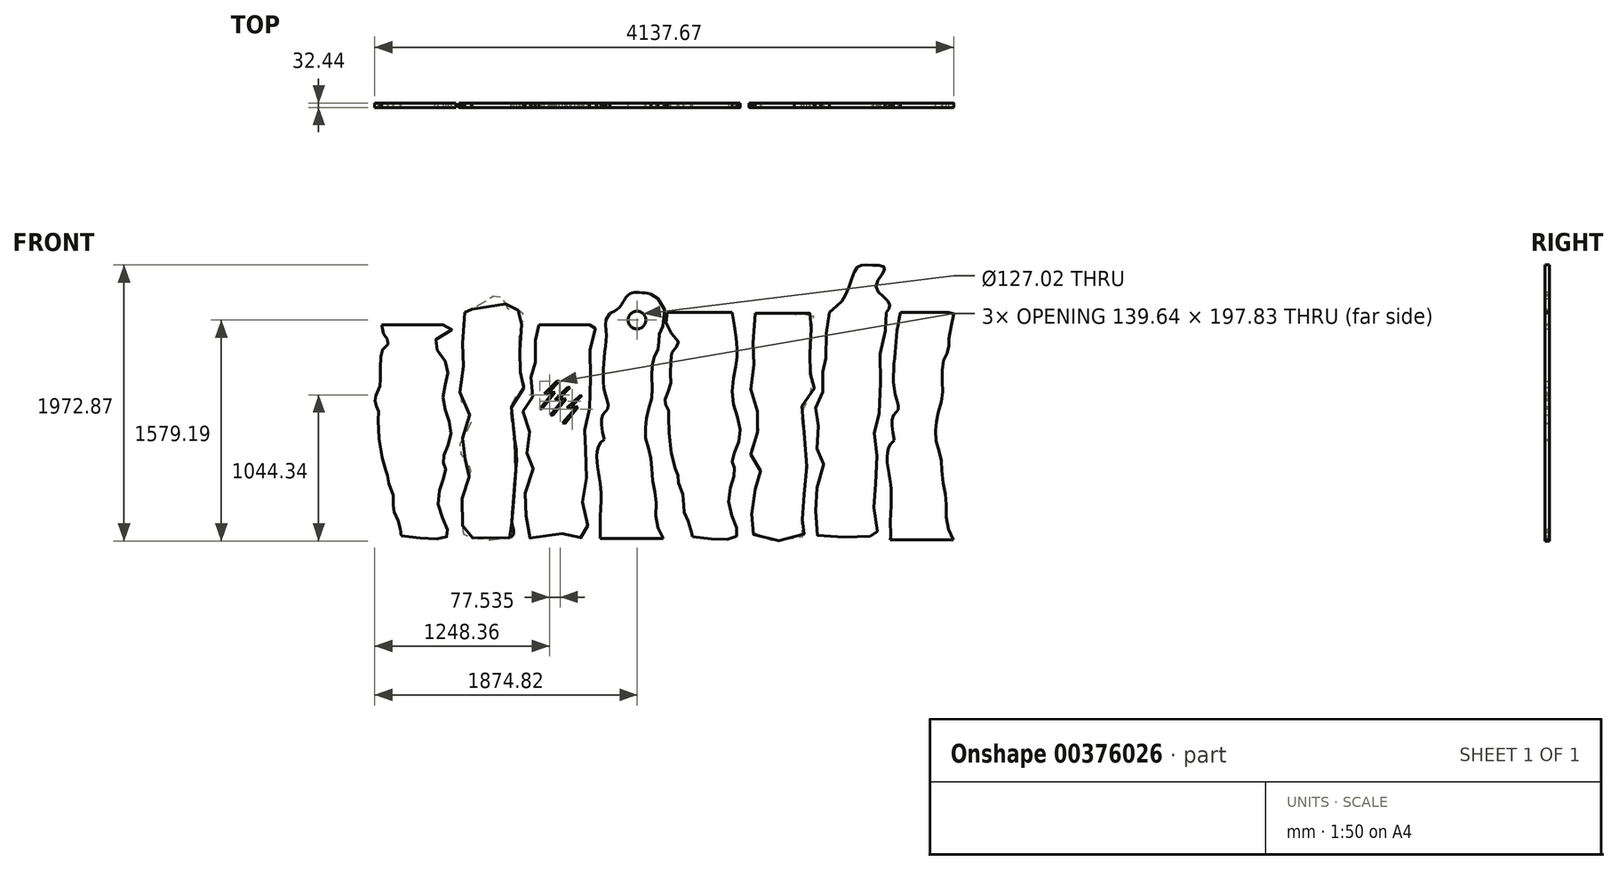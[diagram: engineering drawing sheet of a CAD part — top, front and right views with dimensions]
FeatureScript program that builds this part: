
annotation { "Feature Type Name" : "Feature", "Feature Type Description" : "" }
export const myFeature = defineFeature(function(context is Context, id is Id, definition is map)
    precondition{}
    {
        {
            var Q0;
            Q0=qCreatedBy(makeId("Front.planeOp"),FACE);
            var sketch = newSketch(context, id + "F0", { "sketchPlane" : qUnion([Q0])});
            skFitSpline(sketch, "E0", {"points": [v(-541.96, 281.1) * mm, v(-507.6, 158.34) * mm, v(-472.77, 104.36) * mm, v(-472.77, 70.55) * mm, v(-536.18, 0) * mm, v(-555.2, -90.1) * mm, v(-557.32, -301.45) * mm, v(-561.55, -390.23) * mm, v(-618.62, -523.39) * mm, v(-616.5, -555.1) * mm, v(-608.05, -599.48) * mm, v(-578.46, -660.77) * mm, v(-580.57, -730.52) * mm, v(-527.79, -1239.7) * mm, v(-480.03, -1362.86) * mm, v(-480.03, -1413.13) * mm, v(-412.16, -1626.78) * mm, v(-417.19, -1739.89) * mm, v(-379.49, -1832.9) * mm, v(-337.02, -1971.17) * mm, v(-341.75, -1975.56) * mm], "startDerivative": vector(-372.56, -2835.6) * mm, "endDerivative": vector(-506.02, -138.97) * mm});
            skLineSegment(sketch, "E1", {"start": v(-541.96, 281.1) * mm, "end": v(131.63, 281.1) * mm});
            skFitSpline(sketch, "E2", {"points": [v(131.63, 281.1) * mm, v(103, 164.5) * mm, v(170.93, -145.04) * mm, v(131.63, -522.75) * mm, v(220.27, -918.68) * mm, v(131.63, -1205.86) * mm, v(161.94, -1317.66) * mm, v(76.13, -1680.41) * mm, v(184.95, -2037.45) * mm, v(-326.9, -2043.6) * mm], "startDerivative": vector(12193.25, 0) * mm, "endDerivative": vector(-4963.23, 655.32) * mm});
            skLineSegment(sketch, "E3", {"start": v(-326.9, -2043.6) * mm, "end": v(-337.02, -1971.17) * mm});
            skLineSegment(sketch, "E4", {"start": v(-1646.42, 409.32) * mm, "end": v(-1646.42, -1190.68) * mm});
            skFitSpline(sketch, "E5", {"points": [v(371.94, 415.21) * mm, v(347.86, 0) * mm, v(355.89, -226.97) * mm, v(331.8, -556.08) * mm, v(444.19, -780.84) * mm, v(307.73, -1077.85) * mm, v(420.1, -1262.47) * mm, v(412.08, -1415) * mm, v(339.84, -1655.8) * mm, v(347.86, -1968.87) * mm, v(388, -2049.14) * mm, v(893.71, -2049.14) * mm, v(893.71, -1920.7) * mm, v(893.71, -1832.4) * mm, v(925.82, -1431.05) * mm, v(933.85, -1069.82) * mm, v(901.74, -564.1) * mm, v(1030.17, -395.54) * mm, v(990.04, -275.13) * mm, v(982.01, -106.56) * mm, v(982.01, 214.53) * mm, v(1014.12, 399.16) * mm, v(915.42, 447.26) * mm, v(834.92, 467.15) * mm, v(451.6, 447.77) * mm], "startDerivative": vector(-753, -7908.25) * mm, "endDerivative": vector(-21721.49, -16904.44) * mm});
            skLineSegment(sketch, "E6", {"start": v(451.6, 447.77) * mm, "end": v(371.94, 415.21) * mm});
            skFitSpline(sketch, "E7", {"points": [v(1189.54, 281.1) * mm, v(1159.24, 203.5) * mm, v(1151.66, -91.99) * mm, v(1136.5, -175.33) * mm, v(1098.62, -342.02) * mm, v(1113.78, -531.43) * mm, v(1015.28, -667.81) * mm, v(1083.47, -887.54) * mm, v(1053.16, -1130) * mm, v(1128.93, -1258.8) * mm, v(1038, -1561.86) * mm, v(1045.59, -1834.62) * mm, v(1106.2, -2077.08) * mm, v(1613.84, -2008.88) * mm, v(1659.3, -2077.08) * mm, v(1727.49, -1940.7) * mm, v(1666.87, -1645.2) * mm, v(1727.49, -1326.98) * mm, v(1682.03, -955.73) * mm, v(1712.33, -819.35) * mm, v(1757.8, -425.36) * mm, v(1750.22, 0) * mm, v(1812.36, 245.6) * mm, v(1818.4, 281.1) * mm, v(1746.43, 281.1) * mm], "startDerivative": vector(-915.93, -4719.56) * mm, "endDerivative": vector(-3660.24, -902.15) * mm});
            skLineSegment(sketch, "E8", {"start": v(1189.54, 281.1) * mm, "end": v(1746.43, 281.1) * mm});
            skPoint(sketch, "E9.1.internal.snap0", {"position": v(1863.87, -2077.08) * mm});
            skPoint(sketch, "E9.2.internal.snap0", {"position": v(1863.87, -2077.08) * mm});
            skFitSpline(sketch, "E9", {"points": [v(1863.87, -2077.08) * mm, v(1863.87, -1849.27) * mm, v(1863.87, -1458.06) * mm, v(1906.48, -981.8) * mm], "startDerivative": vector(45.66, 769.83) * mm, "endDerivative": vector(1037.5, 767.44) * mm});
            skFitSpline(sketch, "E10", {"points": [v(1973.4, 407.8) * mm, v(1932, 191.82) * mm, v(1914.98, 0) * mm, v(1897.98, -224.9) * mm, v(1914.98, -471.54) * mm, v(1949, -641.63) * mm, v(1889.47, -718.17) * mm, v(1906.48, -981.8) * mm], "startDerivative": vector(-1553.65, -1644.93) * mm, "endDerivative": vector(397.57, -1910.23) * mm});
            skLineSegment(sketch, "E11", {"start": v(2501.34, 569.02) * mm, "end": v(2422.34, 618.83) * mm});
            skLineSegment(sketch, "E12", {"start": v(1863.87, -2077.08) * mm, "end": v(2558.46, -2077.08) * mm});
            skFitSpline(sketch, "E13", {"points": [v(2558.46, -2077.08) * mm, v(2482.3, -1887.01) * mm, v(2477.8, -1657.25) * mm, v(2450.77, -1486.06) * mm, v(2428.25, -1269.81) * mm, v(2414.73, -1148.17) * mm, v(2365.18, -981.49) * mm, v(2365.18, -832.82) * mm, v(2378.7, -711.18) * mm, v(2428.25, -544.5) * mm, v(2437.26, -391.32) * mm, v(2432.75, -206.6) * mm, v(2459.78, -75.96) * mm, v(2495.83, 0) * mm, v(2509.34, 90.73) * mm, v(2513.85, 176.33) * mm, v(2558.46, 281.1) * mm, v(2501.34, 569.02) * mm], "startDerivative": vector(-1595.21, 2626.65) * mm, "endDerivative": vector(-3204.2, 0) * mm});
            skFitSpline(sketch, "E14", {"points": [v(2604.53, 413.66) * mm, v(2602.42, 258.18) * mm, v(2725.01, 93.31) * mm, v(2725.01, 59.5) * mm, v(2661.6, -11.05) * mm, v(2642.58, -101.14) * mm, v(2640.47, -312.5) * mm, v(2636.24, -401.28) * mm, v(2579.17, -534.44) * mm, v(2581.28, -566.14) * mm, v(2589.74, -610.53) * mm, v(2619.33, -671.82) * mm, v(2617.22, -741.58) * mm, v(2670, -1250.74) * mm, v(2717.76, -1373.9) * mm, v(2717.76, -1424.18) * mm, v(2785.62, -1637.83) * mm, v(2780.6, -1750.94) * mm, v(2818.3, -1843.94) * mm, v(2861.03, -1982.19) * mm, v(2856.04, -1986.61) * mm], "startDerivative": vector(-632.65, -2426.74) * mm, "endDerivative": vector(-506.02, -138.97) * mm});
            skLineSegment(sketch, "E15", {"start": v(2604.53, 413.66) * mm, "end": v(3318.88, 413.66) * mm});
            skFitSpline(sketch, "E16", {"points": [v(3318.88, 413.66) * mm, v(3370.75, 44.31) * mm, v(3362.77, -151.2) * mm, v(3318.88, -530.25) * mm, v(3406.66, -929.25) * mm, v(3318.88, -1216.54) * mm, v(3346.81, -1332.25) * mm, v(3278.98, -1691.35) * mm, v(3370.75, -2038.48) * mm, v(2879.98, -2054.44) * mm], "startDerivative": vector(551.1, -3340.09) * mm, "endDerivative": vector(-4963.23, 655.32) * mm});
            skLineSegment(sketch, "E17", {"start": v(2879.98, -2054.44) * mm, "end": v(2861.03, -1982.19) * mm});
            skFitSpline(sketch, "E18", {"points": [v(3569.73, 404.16) * mm, v(3545.65, -11.05) * mm, v(3553.68, -238.02) * mm, v(3529.6, -567.13) * mm, v(3641.97, -791.9) * mm, v(3505.51, -1088.9) * mm, v(3617.9, -1273.53) * mm, v(3609.87, -1426.04) * mm, v(3537.62, -1666.86) * mm, v(3545.65, -1979.92) * mm, v(3585.78, -2060.2) * mm, v(4091.5, -2060.2) * mm, v(4091.5, -1931.76) * mm, v(4091.5, -1843.46) * mm, v(4123.6, -1442.1) * mm, v(4131.63, -1080.87) * mm, v(4099.53, -575.16) * mm, v(4227.96, -406.59) * mm, v(4187.82, -286.18) * mm, v(4179.8, -117.6) * mm, v(4179.8, 203.48) * mm, v(4211.9, 388.1) * mm, v(4035.3, 404.16) * mm, v(4003.2, 404.16) * mm, v(4011.23, 404.16) * mm], "startDerivative": vector(-753, -7908.25) * mm, "endDerivative": vector(1414.6, -17.02) * mm});
            skLineSegment(sketch, "E19", {"start": v(4011.23, 404.16) * mm, "end": v(3569.73, 404.16) * mm});
            skFitSpline(sketch, "E20", {"points": [v(4387.33, 413.66) * mm, v(4357.02, 192.45) * mm, v(4349.45, -103.04) * mm, v(4334.3, -186.38) * mm, v(4296.4, -353.07) * mm, v(4311.56, -542.48) * mm, v(4213.07, -678.86) * mm, v(4281.26, -898.59) * mm, v(4250.95, -1141.04) * mm, v(4326.72, -1269.84) * mm, v(4235.8, -1572.91) * mm, v(4243.37, -1845.67) * mm, v(4303.99, -2088.12) * mm, v(4811.62, -2019.93) * mm, v(4857.08, -2088.12) * mm, v(4925.27, -1951.74) * mm, v(4864.66, -1656.25) * mm, v(4925.27, -1338.03) * mm, v(4879.81, -966.78) * mm, v(4910.12, -830.4) * mm, v(4955.58, -436.41) * mm, v(4948, -11.05) * mm, v(5016.2, 260.64) * mm, v(5016.2, 413.66) * mm, v(4944.21, 413.66) * mm], "startDerivative": vector(-915.93, -4719.56) * mm, "endDerivative": vector(-3660.24, -902.15) * mm});
            skPoint(sketch, "E21.1.internal.snap0", {"position": v(5061.65, -2088.12) * mm});
            skPoint(sketch, "E21.2.internal.snap0", {"position": v(5061.65, -2088.12) * mm});
            skFitSpline(sketch, "E21", {"points": [v(5061.65, -2088.12) * mm, v(5061.65, -1860.32) * mm, v(5061.65, -1469.11) * mm, v(5104.27, -992.86) * mm], "startDerivative": vector(45.66, 769.83) * mm, "endDerivative": vector(1037.5, 767.44) * mm});
            skFitSpline(sketch, "E22", {"points": [v(5172.3, 413.66) * mm, v(5129.78, 180.77) * mm, v(5112.77, -11.05) * mm, v(5095.76, -235.96) * mm, v(5112.77, -482.59) * mm, v(5146.79, -652.68) * mm, v(5087.26, -729.22) * mm, v(5104.27, -992.86) * mm], "startDerivative": vector(-323.99, -1499.1) * mm, "endDerivative": vector(397.57, -1910.23) * mm});
            skLineSegment(sketch, "E23", {"start": v(5699.58, 413.66) * mm, "end": v(5172.3, 413.66) * mm});
            skLineSegment(sketch, "E24", {"start": v(5061.65, -2088.12) * mm, "end": v(5756.32, -2088.12) * mm});
            skFitSpline(sketch, "E25", {"points": [v(5756.32, -2088.12) * mm, v(5680.1, -1898.07) * mm, v(5675.6, -1668.3) * mm, v(5648.56, -1497.1) * mm, v(5626.03, -1280.86) * mm, v(5612.52, -1159.23) * mm, v(5562.96, -992.54) * mm, v(5562.96, -843.87) * mm, v(5576.48, -722.23) * mm, v(5626.03, -555.54) * mm, v(5635.04, -402.37) * mm, v(5630.54, -217.66) * mm, v(5657.57, -87) * mm, v(5693.61, -11.05) * mm, v(5707.13, 79.68) * mm, v(5711.63, 165.28) * mm, v(5756.32, 413.66) * mm, v(5699.58, 413.66) * mm], "startDerivative": vector(-1595.21, 2626.65) * mm, "endDerivative": vector(-3204.22, 0) * mm});
            skFitSpline(sketch, "E26", {"points": [v(1973.4, 407.8) * mm, v(2072.73, 467.4) * mm, v(2132.33, 558.22) * mm, v(2207.53, 627.75) * mm, v(2422.34, 618.83) * mm], "startDerivative": vector(468.92, 213.8) * mm, "endDerivative": vector(767.44, -125.53) * mm});
            skCircle(sketch, "E27", {"center": v(2269.64, 331.5) * mm, "radius": 97.88 * mm});
            skLineSegment(sketch, "E28", {"start": v(1383.71, -342.02) * mm, "end": v(1245.99, -478.3) * mm});
            skLineSegment(sketch, "E29", {"start": v(1245.99, -478.3) * mm, "end": v(1329.91, -484.76) * mm});
            skLineSegment(sketch, "E30", {"start": v(1329.91, -484.76) * mm, "end": v(1196.5, -644) * mm});
            skLineSegment(sketch, "E31", {"start": v(1196.5, -644) * mm, "end": v(1223.52, -645.3) * mm});
            skLineSegment(sketch, "E32", {"start": v(1223.52, -645.3) * mm, "end": v(1367.38, -467.05) * mm});
            skLineSegment(sketch, "E33", {"start": v(1367.38, -467.05) * mm, "end": v(1294.1, -462.53) * mm});
            skLineSegment(sketch, "E34", {"start": v(1294.1, -462.53) * mm, "end": v(1411.72, -340.38) * mm});
            skLineSegment(sketch, "E35", {"start": v(1411.72, -340.38) * mm, "end": v(1383.71, -342.02) * mm});
            skLineSegment(sketch, "E36", {"start": v(1503.21, -411.76) * mm, "end": v(1365.49, -548.05) * mm});
            skLineSegment(sketch, "E37", {"start": v(1365.49, -548.05) * mm, "end": v(1449.41, -554.5) * mm});
            skLineSegment(sketch, "E38", {"start": v(1449.41, -554.5) * mm, "end": v(1316, -713.75) * mm});
            skLineSegment(sketch, "E39", {"start": v(1316, -713.75) * mm, "end": v(1343.02, -715.04) * mm});
            skLineSegment(sketch, "E40", {"start": v(1343.02, -715.04) * mm, "end": v(1486.88, -536.8) * mm});
            skLineSegment(sketch, "E41", {"start": v(1486.88, -536.8) * mm, "end": v(1413.6, -532.28) * mm});
            skLineSegment(sketch, "E42", {"start": v(1413.6, -532.28) * mm, "end": v(1531.22, -410.13) * mm});
            skLineSegment(sketch, "E43", {"start": v(1531.22, -410.13) * mm, "end": v(1503.21, -411.76) * mm});
            skLineSegment(sketch, "E44", {"start": v(1636.63, -501.91) * mm, "end": v(1498.9, -638.2) * mm});
            skLineSegment(sketch, "E45", {"start": v(1498.9, -638.2) * mm, "end": v(1582.83, -644.65) * mm});
            skLineSegment(sketch, "E46", {"start": v(1582.83, -644.65) * mm, "end": v(1449.41, -803.9) * mm});
            skLineSegment(sketch, "E47", {"start": v(1449.41, -803.9) * mm, "end": v(1476.44, -805.19) * mm});
            skLineSegment(sketch, "E48", {"start": v(1476.44, -805.19) * mm, "end": v(1620.3, -626.95) * mm});
            skLineSegment(sketch, "E49", {"start": v(1620.3, -626.95) * mm, "end": v(1547.01, -622.42) * mm});
            skLineSegment(sketch, "E50", {"start": v(1547.01, -622.42) * mm, "end": v(1664.64, -500.28) * mm});
            skLineSegment(sketch, "E51", {"start": v(1664.64, -500.28) * mm, "end": v(1636.63, -501.91) * mm});
            skFitSpline(sketch, "E52", {"points": [v(4387.33, 413.66) * mm, v(4540.36, 560.16) * mm, v(4692.36, 907.6) * mm, v(4829.89, 936.55) * mm, v(4999.99, 903.97) * mm, v(4902.27, 697.69) * mm, v(5050.65, 520.35) * mm, v(5016.2, 413.66) * mm], "startDerivative": vector(701.71, 838.72) * mm, "endDerivative": vector(-736.4, -988.67) * mm});
            skSolve(sketch);
        }
        {
            var Q0;
            {var subQ0=sQuery(id+"F0.wireOp",EDGE,"E1");Q0=makeQuery(id+"F0.imprint","IMPRINT",FACE,{"disambiguationData":[TD([[makeQuery(id+"F0.imprint","IMPRINT",EDGE,{"derivedFrom":subQ0}),-1.0]])]});}
            var Q1;
            {var subQ0=sQuery(id+"F0.wireOp",EDGE,"E6");var subQ1=sQuery(id+"F0.wireOp",EDGE,"E5");var subQ2=makeQuery(id+"F0.imprint","INTERSECT",VERTEX,{"disambiguationData":[OD(0.0)],"derivedFrom":[subQ1,subQ0]});Q1=makeQuery(id+"F0.imprint","IMPRINT",FACE,{"disambiguationData":[TD([[makeQuery(id+"F0.imprint","IMPRINT",EDGE,{"disambiguationData":[TD([[subQ2,-1.0]])],"derivedFrom":subQ1}),1.0]])]});}
            var Q2;
            Q2=makeQuery(id+"F0.imprint","IMPRINT",FACE,{"disambiguationData":[TD([[makeQuery(id+"F0.imprint","IMPRINT",EDGE,{"derivedFrom":sQuery(id+"F0.wireOp",EDGE,"E7")}),1.0]])]});
            var Q3;
            Q3=makeQuery(id+"F0.imprint","IMPRINT",FACE,{"disambiguationData":[TD([[makeQuery(id+"F0.imprint","IMPRINT",EDGE,{"derivedFrom":sQuery(id+"F0.wireOp",EDGE,"E9")}),-1.0]])]});
            var Q4;
            {var subQ0=sQuery(id+"F0.wireOp",EDGE,"E15");Q4=makeQuery(id+"F0.imprint","IMPRINT",FACE,{"disambiguationData":[TD([[makeQuery(id+"F0.imprint","IMPRINT",EDGE,{"derivedFrom":subQ0}),-1.0]])]});}
            var Q5;
            {var subQ0=sQuery(id+"F0.wireOp",EDGE,"E19");var subQ1=sQuery(id+"F0.wireOp",EDGE,"E18");var subQ2=makeQuery(id+"F0.imprint","INTERSECT",VERTEX,{"disambiguationData":[OD(0.0)],"derivedFrom":[subQ1,subQ0]});Q5=makeQuery(id+"F0.imprint","IMPRINT",FACE,{"disambiguationData":[TD([[makeQuery(id+"F0.imprint","IMPRINT",EDGE,{"disambiguationData":[TD([[subQ2,-1.0]])],"derivedFrom":subQ1}),1.0]])]});}
            var Q6;
            Q6=makeQuery(id+"F0.imprint","IMPRINT",FACE,{"disambiguationData":[TD([[makeQuery(id+"F0.imprint","IMPRINT",EDGE,{"derivedFrom":sQuery(id+"F0.wireOp",EDGE,"E20")}),1.0]])]});
            var Q7;
            Q7=makeQuery(id+"F0.imprint","IMPRINT",FACE,{"disambiguationData":[TD([[makeQuery(id+"F0.imprint","IMPRINT",EDGE,{"derivedFrom":sQuery(id+"F0.wireOp",EDGE,"E21")}),-1.0]])]});
            extrude(context, id + "F1", {"entities" : qUnion([Q0, Q1, Q2, Q3, Q4, Q5, Q6, Q7]), "depth" : 50 * mm, "offsetDistance" : 25 * mm});
        }
        {
            var Q0;
            Q0=makeQuery(id+"F1.opExtrude","SWEPT_BODY",BODY,{"disambiguationData":[OSD([sQuery(id+"F0.wireOp",EDGE,"E21"),sQuery(id+"F0.wireOp",EDGE,"E22"),sQuery(id+"F0.wireOp",EDGE,"E23"),sQuery(id+"F0.wireOp",EDGE,"E24"),sQuery(id+"F0.wireOp",EDGE,"E25")])]});
            var Q1;
            Q1=makeQuery(id+"F1.opExtrude","SWEPT_BODY",BODY,{"disambiguationData":[OSD([sQuery(id+"F0.wireOp",EDGE,"E20"),sQuery(id+"F0.wireOp",EDGE,"f41024a2-b2b3-4750-a2d3-9d62d5d6f698")])]});
            var Q2;
            Q2=makeQuery(id+"F1.opExtrude","SWEPT_BODY",BODY,{"disambiguationData":[OSD([sQuery(id+"F0.wireOp",EDGE,"E18"),sQuery(id+"F0.wireOp",EDGE,"E19")])]});
            var Q3;
            Q3=makeQuery(id+"F1.opExtrude","SWEPT_BODY",BODY,{"disambiguationData":[OSD([sQuery(id+"F0.wireOp",EDGE,"E14"),sQuery(id+"F0.wireOp",EDGE,"E15"),sQuery(id+"F0.wireOp",EDGE,"E16"),sQuery(id+"F0.wireOp",EDGE,"E17")])]});
            var Q4;
            Q4=makeQuery(id+"F1.opExtrude","SWEPT_BODY",BODY,{"disambiguationData":[OSD([sQuery(id+"F0.wireOp",EDGE,"E9"),sQuery(id+"F0.wireOp",EDGE,"E10"),sQuery(id+"F0.wireOp",EDGE,"E11"),sQuery(id+"F0.wireOp",EDGE,"E12"),sQuery(id+"F0.wireOp",EDGE,"E13")])]});
            var Q5;
            Q5=makeQuery(id+"F1.opExtrude","SWEPT_BODY",BODY,{"disambiguationData":[OSD([sQuery(id+"F0.wireOp",EDGE,"E5"),sQuery(id+"F0.wireOp",EDGE,"E6")])]});
            var Q6;
            Q6=makeQuery(id+"F1.opExtrude","SWEPT_BODY",BODY,{"disambiguationData":[OSD([sQuery(id+"F0.wireOp",EDGE,"E7"),sQuery(id+"F0.wireOp",EDGE,"E8")])]});
            var Q7;
            Q7=makeQuery(id+"F1.opExtrude","SWEPT_BODY",BODY,{"disambiguationData":[OSD([sQuery(id+"F0.wireOp",EDGE,"E0"),sQuery(id+"F0.wireOp",EDGE,"E1"),sQuery(id+"F0.wireOp",EDGE,"E2"),sQuery(id+"F0.wireOp",EDGE,"E3")])]});
            var Q8;
            Q8=makeQuery(id+"F1.opExtrude","CAP_VERTEX",VERTEX,{"disambiguationData":[OSD([sQuery(id+"F0.wireOp",EDGE,"E1"),sQuery(id+"F0.wireOp",EDGE,"E2")])],"isStart":false});
            transform(context, id + "F2", {"entities" : qUnion([Q0, Q1, Q2, Q3, Q4, Q5, Q6, Q7]), "transformType" : TransformType.SCALE_UNIFORMLY, "scale" : 1.6 / 2.47, "scalePoint" : qUnion([Q8]), "makeCopy" : false});
        }
    });
